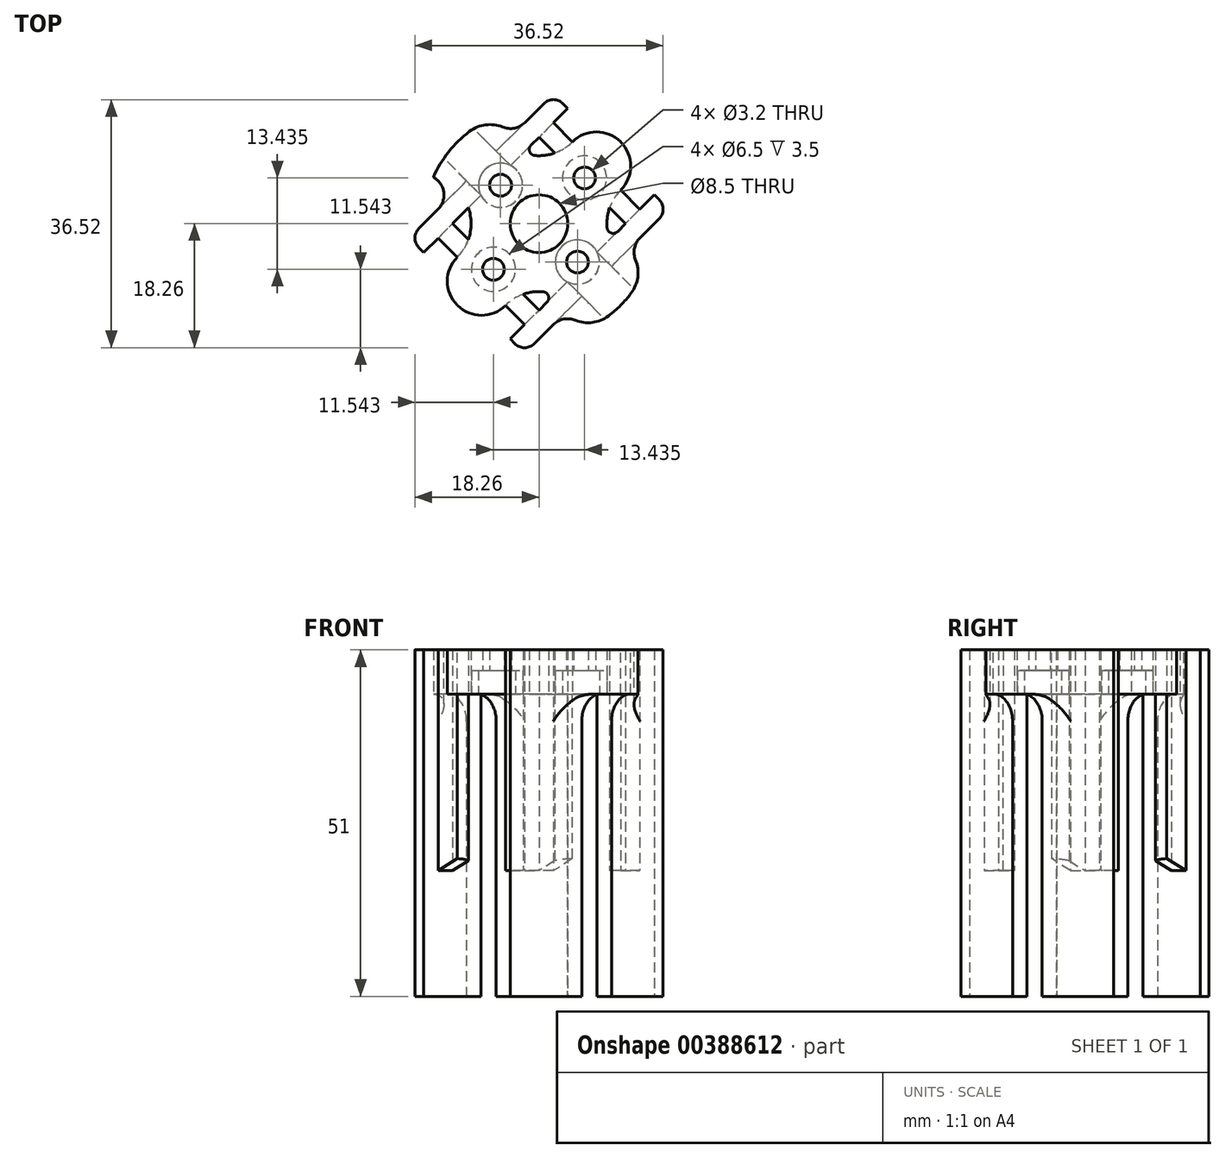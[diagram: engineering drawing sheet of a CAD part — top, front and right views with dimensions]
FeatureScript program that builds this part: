
annotation { "Feature Type Name" : "Feature", "Feature Type Description" : "" }
export const myFeature = defineFeature(function(context is Context, id is Id, definition is map)
    precondition{}
    {
        {
            assignVariable(context, id + "F0", {"name" : "wrapAroundLength", "anyValue" : 46});
        }
        {
            assignVariable(context, id + "F1", {"name" : "screwHeadDepth", "anyValue" : 3.5});
        }
        {
            var Q0;
            Q0=qCreatedBy(makeId("Top.planeOp"),FACE);
            var sketch = newSketch(context, id + "F2", { "sketchPlane" : qUnion([Q0])});
            skCircle(sketch, "E0", {"center": v(0, 0) * mm, "radius": 17 * mm});
            skLineSegment(sketch, "E1", {"start": v(0, 0) * mm, "end": v(-12.02, -12.02) * mm});
            skLineSegment(sketch, "E2", {"start": v(0, 0) * mm, "end": v(12.02, -12.02) * mm});
            skLineSegment(sketch, "E3", {"start": v(0, 0) * mm, "end": v(-12.02, 12.02) * mm});
            skLineSegment(sketch, "E4", {"start": v(0, 0) * mm, "end": v(12.02, 12.02) * mm});
            skCircle(sketch, "E5", {"center": v(-6.72, -6.72) * mm, "radius": 1.6 * mm});
            skCircle(sketch, "E6", {"center": v(6.72, 6.72) * mm, "radius": 1.6 * mm});
            skCircle(sketch, "E7", {"center": v(5.66, -5.66) * mm, "radius": 1.6 * mm});
            skCircle(sketch, "E8", {"center": v(-5.66, 5.66) * mm, "radius": 1.6 * mm});
            skCircle(sketch, "E9", {"center": v(0, 0) * mm, "radius": 4.25 * mm});
            skArc(sketch, "E10", {"start": v(-6.85, 15.56) * mm, "mid": v(0, 10) * mm, "end": v(6.85, 15.56) * mm});
            skArc(sketch, "E11", {"start": v(15.56, 6.85) * mm, "mid": v(10, 0) * mm, "end": v(15.56, -6.85) * mm});
            skArc(sketch, "E12", {"start": v(6.85, -15.56) * mm, "mid": v(0, -10) * mm, "end": v(-6.85, -15.56) * mm});
            skArc(sketch, "E13", {"start": v(-15.56, -6.85) * mm, "mid": v(-10, 0) * mm, "end": v(-15.56, 6.85) * mm});
            skSolve(sketch);
        }
        {
            var Q0;
            {var subQ10=sQuery(id+"F2.wireOp",EDGE,"E11");Q0=makeQuery(id+"F2.imprint","IMPRINT",FACE,{"disambiguationData":[TD([[makeQuery(id+"F2.imprint","IMPRINT",EDGE,{"derivedFrom":subQ10}),-1.0]])]});}
            var Q1;
            {var subQ7=sQuery(id+"F2.wireOp",EDGE,"E10");Q1=makeQuery(id+"F2.imprint","IMPRINT",FACE,{"disambiguationData":[TD([[makeQuery(id+"F2.imprint","IMPRINT",EDGE,{"derivedFrom":subQ7}),-1.0]])]});}
            var Q2;
            {var subQ7=sQuery(id+"F2.wireOp",EDGE,"pa5JDaWK-p0si-kU4j-njws-uxYAEp68zFFt");Q2=makeQuery(id+"F2.imprint","IMPRINT",FACE,{"disambiguationData":[TD([[makeQuery(id+"F2.imprint","IMPRINT",EDGE,{"derivedFrom":subQ7}),-1.0]])]});}
            var Q3;
            {var subQ10=sQuery(id+"F2.wireOp",EDGE,"E12");Q3=makeQuery(id+"F2.imprint","IMPRINT",FACE,{"disambiguationData":[TD([[makeQuery(id+"F2.imprint","IMPRINT",EDGE,{"derivedFrom":subQ10}),-1.0]])]});}
            var Q4;
            {var subQ7=sQuery(id+"F2.wireOp",EDGE,"E13");Q4=makeQuery(id+"F2.imprint","IMPRINT",FACE,{"disambiguationData":[TD([[makeQuery(id+"F2.imprint","IMPRINT",EDGE,{"derivedFrom":subQ7}),-1.0]])]});}
            extrude(context, id + "F3", {"entities" : qUnion([Q0, Q1, Q2, Q3, Q4]), "depth" : (getVariable(context, 'screwHeadDepth')) * mm + 3 * mm});
        }
        {
            var Q0;
            Q0=makeQuery(id+"F3.opExtrude","CAP_FACE",FACE,{"disambiguationData":[OSD([sQuery(id+"F2.wireOp",EDGE,"E0"),sQuery(id+"F2.wireOp",EDGE,"E5"),sQuery(id+"F2.wireOp",EDGE,"E6"),sQuery(id+"F2.wireOp",EDGE,"E7"),sQuery(id+"F2.wireOp",EDGE,"E8"),sQuery(id+"F2.wireOp",EDGE,"E9")])],"isStart":true});
            var sketch = newSketch(context, id + "F4", { "sketchPlane" : qUnion([Q0])});
            skCircle(sketch, "E14", {"center": v(-6.72, 6.72) * mm, "radius": 3.25 * mm});
            skCircle(sketch, "E15", {"center": v(-5.66, -5.66) * mm, "radius": 3.25 * mm});
            skCircle(sketch, "E16", {"center": v(5.66, 5.66) * mm, "radius": 3.25 * mm});
            skCircle(sketch, "E17", {"center": v(6.72, -6.72) * mm, "radius": 3.25 * mm});
            skSolve(sketch);
        }
        {
            var Q0;
            Q0=qSketchRegion(id+"F4",true);
            extrude(context, id + "F5", {"entities" : qUnion([Q0]), "operationType" : NewBodyOperationType.REMOVE, "oppositeDirection" : true, "depth" : (getVariable(context, 'screwHeadDepth')) * mm});
        }
        {
            var Q0;
            Q0=qCreatedBy(makeId("Top.planeOp"),FACE);
            var sketch = newSketch(context, id + "F6", { "sketchPlane" : qUnion([Q0])});
            skLineSegment(sketch, "E18", {"start": v(-5.97, 5.97) * mm, "end": v(-5.97, 5.97) * mm});
            skLineSegment(sketch, "E19", {"start": v(0, 0) * mm, "end": v(-34.06, 34.06) * mm, "construction": true});
            skLineSegment(sketch, "E20", {"start": v(0, 0) * mm, "end": v(34.06, -34.06) * mm, "construction": true});
            skLineSegment(sketch, "E21", {"start": v(0, 0) * mm, "end": v(25.74, 25.74) * mm, "construction": true});
            skLineSegment(sketch, "E22", {"start": v(0, 0) * mm, "end": v(-25.74, -25.74) * mm, "construction": true});
            skLineSegment(sketch, "E23", {"start": v(-8.55, 4.18) * mm, "end": v(-16.97, -4.24) * mm});
            skLineSegment(sketch, "E24", {"start": v(-16.97, -4.24) * mm, "end": v(-19.1, -2.12) * mm});
            skLineSegment(sketch, "E25", {"start": v(-19.1, -2.12) * mm, "end": v(-10.67, 6.3) * mm});
            skCircle(sketch, "E26.0", {"center": v(-5.66, 5.66) * mm, "radius": 3.25 * mm});
            skLineSegment(sketch, "E27.MirrorCS", {"start": v(2.12, 19.1) * mm, "end": v(-6.3, 10.67) * mm});
            skLineSegment(sketch, "E28.MirrorCS", {"start": v(-4.18, 8.55) * mm, "end": v(4.24, 16.97) * mm});
            skLineSegment(sketch, "E29.MirrorCS", {"start": v(4.24, 16.97) * mm, "end": v(2.12, 19.1) * mm});
            skLineSegment(sketch, "E30.MirrorCS", {"start": v(4.18, -8.55) * mm, "end": v(-4.24, -16.97) * mm});
            skLineSegment(sketch, "E31.MirrorCS", {"start": v(-4.24, -16.97) * mm, "end": v(-2.12, -19.1) * mm});
            skLineSegment(sketch, "E32.MirrorCS", {"start": v(-2.12, -19.1) * mm, "end": v(6.3, -10.67) * mm});
            skLineSegment(sketch, "E33.MirrorCS", {"start": v(19.1, 2.12) * mm, "end": v(10.67, -6.3) * mm});
            skLineSegment(sketch, "E34.MirrorCS", {"start": v(8.55, -4.18) * mm, "end": v(16.97, 4.24) * mm});
            skLineSegment(sketch, "E35.MirrorCS", {"start": v(16.97, 4.24) * mm, "end": v(19.1, 2.12) * mm});
            skCircle(sketch, "E36.0", {"center": v(5.66, -5.66) * mm, "radius": 3.25 * mm});
            skLineSegment(sketch, "E37", {"start": v(10.67, -6.3) * mm, "end": v(6.3, -10.67) * mm});
            skLineSegment(sketch, "E38", {"start": v(-10.67, 6.3) * mm, "end": v(-6.3, 10.67) * mm});
            skLineSegment(sketch, "E39", {"start": v(-8.55, 4.18) * mm, "end": v(-10.67, 6.3) * mm});
            skLineSegment(sketch, "E40", {"start": v(-6.3, 10.67) * mm, "end": v(-4.18, 8.55) * mm});
            skLineSegment(sketch, "E41", {"start": v(8.55, -4.18) * mm, "end": v(10.67, -6.3) * mm});
            skLineSegment(sketch, "E42", {"start": v(6.3, -10.67) * mm, "end": v(4.18, -8.55) * mm});
            skSolve(sketch);
        }
        {
            var Q0;
            {var subQ0=sQuery(id+"F6.wireOp",EDGE,"E23");Q0=makeQuery(id+"F6.imprint","IMPRINT",FACE,{"disambiguationData":[TD([[makeQuery(id+"F6.imprint","IMPRINT",EDGE,{"derivedFrom":subQ0}),-1.0]])]});}
            var Q1;
            {var subQ0=sQuery(id+"F6.wireOp",EDGE,"E27.MirrorCS");Q1=makeQuery(id+"F6.imprint","IMPRINT",FACE,{"disambiguationData":[TD([[makeQuery(id+"F6.imprint","IMPRINT",EDGE,{"derivedFrom":subQ0}),1.0]])]});}
            var Q2;
            {var subQ0=sQuery(id+"F6.wireOp",EDGE,"E33.MirrorCS");Q2=makeQuery(id+"F6.imprint","IMPRINT",FACE,{"disambiguationData":[TD([[makeQuery(id+"F6.imprint","IMPRINT",EDGE,{"derivedFrom":subQ0}),-1.0]])]});}
            var Q3;
            {var subQ0=sQuery(id+"F6.wireOp",EDGE,"E30.MirrorCS");Q3=makeQuery(id+"F6.imprint","IMPRINT",FACE,{"disambiguationData":[TD([[makeQuery(id+"F6.imprint","IMPRINT",EDGE,{"derivedFrom":subQ0}),1.0]])]});}
            extrude(context, id + "F7", {"entities" : qUnion([Q0, Q1, Q2, Q3]), "operationType" : NewBodyOperationType.ADD, "depth" : (getVariable(context, 'screwHeadDepth')) * mm + 3 * mm, "hasSecondDirection" : true, "secondDirectionOppositeDirection" : true, "secondDirectionDepth" : (getVariable(context, 'wrapAroundLength')) * mm - (getVariable(context, 'screwHeadDepth')) * mm + 2 * mm});
        }
        {
            var Q0;
            Q0=makeQuery(id+"F7.boolean.opBoolean","INTERSECT",EDGE,{"derivedFrom":[makeQuery(id+"F3.opExtrude","SWEPT_FACE",FACE,{"disambiguationData":[OSD([sQuery(id+"F2.wireOp",EDGE,"E11")])]}),makeQuery(id+"F7.opExtrude","SWEPT_FACE",FACE,{"disambiguationData":[OSD([sQuery(id+"F6.wireOp",EDGE,"E33.MirrorCS")])]})]});
            var Q1;
            Q1=makeQuery(id+"F7.boolean.opBoolean","INTERSECT",EDGE,{"derivedFrom":[makeQuery(id+"F3.opExtrude","SWEPT_FACE",FACE,{"disambiguationData":[OSD([sQuery(id+"F2.wireOp",EDGE,"E12")])]}),makeQuery(id+"F7.opExtrude","SWEPT_FACE",FACE,{"disambiguationData":[OSD([sQuery(id+"F6.wireOp",EDGE,"E32.MirrorCS")])]})]});
            var Q2;
            Q2=makeQuery(id+"F7.boolean.opBoolean","INTERSECT",EDGE,{"derivedFrom":[makeQuery(id+"F3.opExtrude","SWEPT_FACE",FACE,{"disambiguationData":[OSD([sQuery(id+"F2.wireOp",EDGE,"E13")])]}),makeQuery(id+"F7.opExtrude","SWEPT_FACE",FACE,{"disambiguationData":[OSD([sQuery(id+"F6.wireOp",EDGE,"E25"),sQuery(id+"F6.wireOp",EDGE,"E27.MirrorCS"),sQuery(id+"F6.wireOp",EDGE,"E38")])]})]});
            var Q3;
            Q3=makeQuery(id+"F7.boolean.opBoolean","INTERSECT",EDGE,{"derivedFrom":[makeQuery(id+"F3.opExtrude","SWEPT_FACE",FACE,{"disambiguationData":[OSD([sQuery(id+"F2.wireOp",EDGE,"E10")])]}),makeQuery(id+"F7.opExtrude","SWEPT_FACE",FACE,{"disambiguationData":[OSD([sQuery(id+"F6.wireOp",EDGE,"E25"),sQuery(id+"F6.wireOp",EDGE,"E27.MirrorCS"),sQuery(id+"F6.wireOp",EDGE,"E38")])]})]});
            fillet(context, id + "F8", {"entities" : qUnion([Q0, Q1, Q2, Q3]), "radius" : 3 * mm, "tangentPropagation" : true, "allowEdgeOverflow" : false});
        }
        {
            var Q0;
            Q0=makeQuery(id+"F7.boolean.opBoolean","INTERSECT",EDGE,{"derivedFrom":[makeQuery(id+"F3.opExtrude","SWEPT_FACE",FACE,{"disambiguationData":[OSD([sQuery(id+"F2.wireOp",EDGE,"E11")])]}),makeQuery(id+"F7.opExtrude","SWEPT_FACE",FACE,{"disambiguationData":[OSD([sQuery(id+"F6.wireOp",EDGE,"E34.MirrorCS")])]})]});
            var Q1;
            Q1=makeQuery(id+"F7.boolean.opBoolean","INTERSECT",EDGE,{"derivedFrom":[makeQuery(id+"F3.opExtrude","SWEPT_FACE",FACE,{"disambiguationData":[OSD([sQuery(id+"F2.wireOp",EDGE,"E12")])]}),makeQuery(id+"F7.opExtrude","SWEPT_FACE",FACE,{"disambiguationData":[OSD([sQuery(id+"F6.wireOp",EDGE,"E30.MirrorCS")])]})]});
            var Q2;
            Q2=makeQuery(id+"F7.boolean.opBoolean","INTERSECT",EDGE,{"derivedFrom":[makeQuery(id+"F3.opExtrude","SWEPT_FACE",FACE,{"disambiguationData":[OSD([sQuery(id+"F2.wireOp",EDGE,"E10")])]}),makeQuery(id+"F7.opExtrude","SWEPT_FACE",FACE,{"disambiguationData":[OSD([sQuery(id+"F6.wireOp",EDGE,"E28.MirrorCS")])]})]});
            var Q3;
            Q3=makeQuery(id+"F7.boolean.opBoolean","INTERSECT",EDGE,{"derivedFrom":[makeQuery(id+"F3.opExtrude","SWEPT_FACE",FACE,{"disambiguationData":[OSD([sQuery(id+"F2.wireOp",EDGE,"pa5JDaWK-p0si-kU4j-njws-uxYAEp68zFFt")])]}),makeQuery(id+"F7.opExtrude","SWEPT_FACE",FACE,{"disambiguationData":[OSD([sQuery(id+"F6.wireOp",EDGE,"E23")])]})]});
            fillet(context, id + "F9", {"entities" : qUnion([Q0, Q1, Q2, Q3]), "radius" : 0.9 * mm, "tangentPropagation" : true, "allowEdgeOverflow" : false});
        }
        {
            var Q0;
            {var subQ0=sQuery(id+"F2.wireOp",EDGE,"E11");var subQ1=sQuery(id+"F2.wireOp",EDGE,"E0");Q0=makeQuery(id+"F3.opExtrude","SWEPT_EDGE",EDGE,{"disambiguationData":[OSD([subQ1,subQ0]),TDD([makeQuery(id+"F2.imprint","INTERSECT",VERTEX,{"disambiguationData":[OD(0.0)],"derivedFrom":[subQ1,subQ0]})])]});}
            var Q1;
            {var subQ0=sQuery(id+"F2.wireOp",EDGE,"E10");var subQ1=sQuery(id+"F2.wireOp",EDGE,"E0");Q1=makeQuery(id+"F3.opExtrude","SWEPT_EDGE",EDGE,{"disambiguationData":[OSD([subQ1,subQ0]),TDD([makeQuery(id+"F2.imprint","INTERSECT",VERTEX,{"disambiguationData":[OD(1.0)],"derivedFrom":[subQ1,subQ0]})])]});}
            var Q2;
            {var subQ0=sQuery(id+"F2.wireOp",EDGE,"E12");var subQ1=sQuery(id+"F2.wireOp",EDGE,"E0");Q2=makeQuery(id+"F3.opExtrude","SWEPT_EDGE",EDGE,{"disambiguationData":[OSD([subQ1,subQ0]),TDD([makeQuery(id+"F2.imprint","INTERSECT",VERTEX,{"disambiguationData":[OD(1.0)],"derivedFrom":[subQ1,subQ0]})])]});}
            var Q3;
            {var subQ0=sQuery(id+"F2.wireOp",EDGE,"pa5JDaWK-p0si-kU4j-njws-uxYAEp68zFFt");var subQ1=sQuery(id+"F2.wireOp",EDGE,"E0");Q3=makeQuery(id+"F3.opExtrude","SWEPT_EDGE",EDGE,{"disambiguationData":[OSD([subQ1,subQ0]),TDD([makeQuery(id+"F2.imprint","INTERSECT",VERTEX,{"disambiguationData":[OD(0.0)],"derivedFrom":[subQ1,subQ0]})])]});}
            var Q4;
            {var subQ0=sQuery(id+"F2.wireOp",EDGE,"E0");var subQ1=makeQuery(id+"F2.imprint","INTERSECT",VERTEX,{"derivedFrom":[subQ0,sQuery(id+"F2.wireOp",EDGE,"E2")]});var subQ2=sQuery(id+"F2.wireOp",EDGE,"E11");Q4=makeQuery(id+"F8.opFillet","BLEND_EDGE",EDGE,{"blendedFrom":[makeQuery(id+"F7.boolean.opBoolean","INTERSECT",EDGE,{"derivedFrom":[makeQuery(id+"F3.opExtrude","SWEPT_FACE",FACE,{"disambiguationData":[OSD([subQ2])]}),makeQuery(id+"F7.opExtrude","SWEPT_FACE",FACE,{"disambiguationData":[OSD([sQuery(id+"F6.wireOp",EDGE,"E33.MirrorCS")])]})]}),makeQuery(id+"F3.opExtrude","SWEPT_FACE",FACE,{"disambiguationData":[OSD([subQ0]),TDD([makeQuery(id+"F2.imprint","IMPRINT",EDGE,{"disambiguationData":[TD([[subQ1,1.0]])],"derivedFrom":subQ0}),makeQuery(id+"F2.imprint","IMPRINT",EDGE,{"disambiguationData":[TD([[subQ1,-1.0]])],"derivedFrom":subQ0})])]})],"blendedInto":[makeQuery(id+"F3.opExtrude","SWEPT_FACE",FACE,{"disambiguationData":[OSD([subQ0]),TDD([makeQuery(id+"F2.imprint","IMPRINT",EDGE,{"disambiguationData":[TD([[subQ1,1.0]])],"derivedFrom":subQ0}),makeQuery(id+"F2.imprint","IMPRINT",EDGE,{"disambiguationData":[TD([[subQ1,-1.0]])],"derivedFrom":subQ0})])]})]});}
            var Q5;
            {var subQ0=sQuery(id+"F2.wireOp",EDGE,"E0");var subQ1=makeQuery(id+"F2.imprint","INTERSECT",VERTEX,{"derivedFrom":[subQ0,sQuery(id+"F2.wireOp",EDGE,"E2")]});var subQ2=sQuery(id+"F2.wireOp",EDGE,"E12");Q5=makeQuery(id+"F8.opFillet","BLEND_EDGE",EDGE,{"blendedFrom":[makeQuery(id+"F7.boolean.opBoolean","INTERSECT",EDGE,{"derivedFrom":[makeQuery(id+"F3.opExtrude","SWEPT_FACE",FACE,{"disambiguationData":[OSD([subQ2])]}),makeQuery(id+"F7.opExtrude","SWEPT_FACE",FACE,{"disambiguationData":[OSD([sQuery(id+"F6.wireOp",EDGE,"E32.MirrorCS")])]})]}),makeQuery(id+"F3.opExtrude","SWEPT_FACE",FACE,{"disambiguationData":[OSD([subQ0]),TDD([makeQuery(id+"F2.imprint","IMPRINT",EDGE,{"disambiguationData":[TD([[subQ1,1.0]])],"derivedFrom":subQ0}),makeQuery(id+"F2.imprint","IMPRINT",EDGE,{"disambiguationData":[TD([[subQ1,-1.0]])],"derivedFrom":subQ0})])]})],"blendedInto":[makeQuery(id+"F3.opExtrude","SWEPT_FACE",FACE,{"disambiguationData":[OSD([subQ0]),TDD([makeQuery(id+"F2.imprint","IMPRINT",EDGE,{"disambiguationData":[TD([[subQ1,1.0]])],"derivedFrom":subQ0}),makeQuery(id+"F2.imprint","IMPRINT",EDGE,{"disambiguationData":[TD([[subQ1,-1.0]])],"derivedFrom":subQ0})])]})]});}
            var Q6;
            {var subQ0=sQuery(id+"F2.wireOp",EDGE,"E0");var subQ1=makeQuery(id+"F2.imprint","INTERSECT",VERTEX,{"derivedFrom":[subQ0,sQuery(id+"F2.wireOp",EDGE,"E3")]});var subQ2=sQuery(id+"F2.wireOp",EDGE,"pa5JDaWK-p0si-kU4j-njws-uxYAEp68zFFt");Q6=makeQuery(id+"F8.opFillet","BLEND_EDGE",EDGE,{"blendedFrom":[makeQuery(id+"F7.boolean.opBoolean","INTERSECT",EDGE,{"derivedFrom":[makeQuery(id+"F3.opExtrude","SWEPT_FACE",FACE,{"disambiguationData":[OSD([subQ2])]}),makeQuery(id+"F7.opExtrude","SWEPT_FACE",FACE,{"disambiguationData":[OSD([sQuery(id+"F6.wireOp",EDGE,"E25")])]})]}),makeQuery(id+"F3.opExtrude","SWEPT_FACE",FACE,{"disambiguationData":[OSD([subQ0]),TDD([makeQuery(id+"F2.imprint","IMPRINT",EDGE,{"disambiguationData":[TD([[subQ1,1.0]])],"derivedFrom":subQ0}),makeQuery(id+"F2.imprint","IMPRINT",EDGE,{"disambiguationData":[TD([[subQ1,-1.0]])],"derivedFrom":subQ0})])]})],"blendedInto":[makeQuery(id+"F3.opExtrude","SWEPT_FACE",FACE,{"disambiguationData":[OSD([subQ0]),TDD([makeQuery(id+"F2.imprint","IMPRINT",EDGE,{"disambiguationData":[TD([[subQ1,1.0]])],"derivedFrom":subQ0}),makeQuery(id+"F2.imprint","IMPRINT",EDGE,{"disambiguationData":[TD([[subQ1,-1.0]])],"derivedFrom":subQ0})])]})]});}
            var Q7;
            {var subQ0=sQuery(id+"F2.wireOp",EDGE,"E0");var subQ1=makeQuery(id+"F2.imprint","INTERSECT",VERTEX,{"derivedFrom":[subQ0,sQuery(id+"F2.wireOp",EDGE,"E3")]});var subQ2=sQuery(id+"F2.wireOp",EDGE,"E10");Q7=makeQuery(id+"F8.opFillet","BLEND_EDGE",EDGE,{"blendedFrom":[makeQuery(id+"F7.boolean.opBoolean","INTERSECT",EDGE,{"derivedFrom":[makeQuery(id+"F3.opExtrude","SWEPT_FACE",FACE,{"disambiguationData":[OSD([subQ2])]}),makeQuery(id+"F7.opExtrude","SWEPT_FACE",FACE,{"disambiguationData":[OSD([sQuery(id+"F6.wireOp",EDGE,"E27.MirrorCS")])]})]}),makeQuery(id+"F3.opExtrude","SWEPT_FACE",FACE,{"disambiguationData":[OSD([subQ0]),TDD([makeQuery(id+"F2.imprint","IMPRINT",EDGE,{"disambiguationData":[TD([[subQ1,1.0]])],"derivedFrom":subQ0}),makeQuery(id+"F2.imprint","IMPRINT",EDGE,{"disambiguationData":[TD([[subQ1,-1.0]])],"derivedFrom":subQ0})])]})],"blendedInto":[makeQuery(id+"F3.opExtrude","SWEPT_FACE",FACE,{"disambiguationData":[OSD([subQ0]),TDD([makeQuery(id+"F2.imprint","IMPRINT",EDGE,{"disambiguationData":[TD([[subQ1,1.0]])],"derivedFrom":subQ0}),makeQuery(id+"F2.imprint","IMPRINT",EDGE,{"disambiguationData":[TD([[subQ1,-1.0]])],"derivedFrom":subQ0})])]})]});}
            var Q8;
            {var subQ0=sQuery(id+"F2.wireOp",EDGE,"E13");var subQ1=sQuery(id+"F2.wireOp",EDGE,"E0");Q8=makeQuery(id+"F3.opExtrude","SWEPT_EDGE",EDGE,{"disambiguationData":[OSD([subQ1,subQ0]),TDD([makeQuery(id+"F2.imprint","INTERSECT",VERTEX,{"disambiguationData":[OD(0.0)],"derivedFrom":[subQ1,subQ0]})])]});}
            fillet(context, id + "F10", {"entities" : qUnion([Q0, Q1, Q2, Q3, Q4, Q5, Q6, Q7, Q8]), "radius" : 5 * mm, "tangentPropagation" : true, "allowEdgeOverflow" : false});
        }
        {
            var Q0;
            Q0=makeQuery(id+"F7.boolean.opBoolean","INTERSECT",EDGE,{"derivedFrom":[makeQuery(id+"F3.opExtrude","CAP_FACE",FACE,{"disambiguationData":[OSD([sQuery(id+"F2.wireOp",EDGE,"E0"),sQuery(id+"F2.wireOp",EDGE,"E5"),sQuery(id+"F2.wireOp",EDGE,"E6"),sQuery(id+"F2.wireOp",EDGE,"E7"),sQuery(id+"F2.wireOp",EDGE,"E8"),sQuery(id+"F2.wireOp",EDGE,"E9"),sQuery(id+"F2.wireOp",EDGE,"E10"),sQuery(id+"F2.wireOp",EDGE,"E11"),sQuery(id+"F2.wireOp",EDGE,"E12"),sQuery(id+"F2.wireOp",EDGE,"E13")])],"isStart":true}),makeQuery(id+"F7.opExtrude","SWEPT_FACE",FACE,{"disambiguationData":[OSD([sQuery(id+"F6.wireOp",EDGE,"E25")])]})]});
            var Q1;
            Q1=makeQuery(id+"F7.boolean.opBoolean","INTERSECT",EDGE,{"derivedFrom":[makeQuery(id+"F3.opExtrude","CAP_FACE",FACE,{"disambiguationData":[OSD([sQuery(id+"F2.wireOp",EDGE,"E0"),sQuery(id+"F2.wireOp",EDGE,"E5"),sQuery(id+"F2.wireOp",EDGE,"E6"),sQuery(id+"F2.wireOp",EDGE,"E7"),sQuery(id+"F2.wireOp",EDGE,"E8"),sQuery(id+"F2.wireOp",EDGE,"E9"),sQuery(id+"F2.wireOp",EDGE,"E10"),sQuery(id+"F2.wireOp",EDGE,"E11"),sQuery(id+"F2.wireOp",EDGE,"E12"),sQuery(id+"F2.wireOp",EDGE,"E13")])],"isStart":true}),makeQuery(id+"F7.opExtrude","SWEPT_FACE",FACE,{"disambiguationData":[OSD([sQuery(id+"F6.wireOp",EDGE,"E27.MirrorCS")])]})]});
            var Q2;
            Q2=makeQuery(id+"F7.boolean.opBoolean","INTERSECT",EDGE,{"derivedFrom":[makeQuery(id+"F3.opExtrude","CAP_FACE",FACE,{"disambiguationData":[OSD([sQuery(id+"F2.wireOp",EDGE,"E0"),sQuery(id+"F2.wireOp",EDGE,"E5"),sQuery(id+"F2.wireOp",EDGE,"E6"),sQuery(id+"F2.wireOp",EDGE,"E7"),sQuery(id+"F2.wireOp",EDGE,"E8"),sQuery(id+"F2.wireOp",EDGE,"E9"),sQuery(id+"F2.wireOp",EDGE,"E10"),sQuery(id+"F2.wireOp",EDGE,"E11"),sQuery(id+"F2.wireOp",EDGE,"E12"),sQuery(id+"F2.wireOp",EDGE,"E13")])],"isStart":true}),makeQuery(id+"F7.opExtrude","SWEPT_FACE",FACE,{"disambiguationData":[OSD([sQuery(id+"F6.wireOp",EDGE,"E32.MirrorCS")])]})]});
            var Q3;
            Q3=makeQuery(id+"F7.boolean.opBoolean","INTERSECT",EDGE,{"derivedFrom":[makeQuery(id+"F3.opExtrude","CAP_FACE",FACE,{"disambiguationData":[OSD([sQuery(id+"F2.wireOp",EDGE,"E0"),sQuery(id+"F2.wireOp",EDGE,"E5"),sQuery(id+"F2.wireOp",EDGE,"E6"),sQuery(id+"F2.wireOp",EDGE,"E7"),sQuery(id+"F2.wireOp",EDGE,"E8"),sQuery(id+"F2.wireOp",EDGE,"E9"),sQuery(id+"F2.wireOp",EDGE,"E10"),sQuery(id+"F2.wireOp",EDGE,"E11"),sQuery(id+"F2.wireOp",EDGE,"E12"),sQuery(id+"F2.wireOp",EDGE,"E13")])],"isStart":true}),makeQuery(id+"F7.opExtrude","SWEPT_FACE",FACE,{"disambiguationData":[OSD([sQuery(id+"F6.wireOp",EDGE,"E33.MirrorCS")])]})]});
            fillet(context, id + "F11", {"entities" : qUnion([Q0, Q1, Q2, Q3]), "radius" : 4 * mm, "tangentPropagation" : true, "allowEdgeOverflow" : false});
        }
        {
            var Q0;
            Q0=makeQuery(id+"F7.opExtrude","SWEPT_EDGE",EDGE,{"disambiguationData":[OSD([sQuery(id+"F6.wireOp",EDGE,"E31.MirrorCS"),sQuery(id+"F6.wireOp",EDGE,"E32.MirrorCS")])]});
            var Q1;
            Q1=makeQuery(id+"F7.opExtrude","SWEPT_EDGE",EDGE,{"disambiguationData":[OSD([sQuery(id+"F6.wireOp",EDGE,"E33.MirrorCS"),sQuery(id+"F6.wireOp",EDGE,"E35.MirrorCS")])]});
            var Q2;
            Q2=makeQuery(id+"F7.opExtrude","SWEPT_EDGE",EDGE,{"disambiguationData":[OSD([sQuery(id+"F6.wireOp",EDGE,"E27.MirrorCS"),sQuery(id+"F6.wireOp",EDGE,"E29.MirrorCS")])]});
            var Q3;
            Q3=makeQuery(id+"F7.opExtrude","SWEPT_EDGE",EDGE,{"disambiguationData":[OSD([sQuery(id+"F6.wireOp",EDGE,"E24"),sQuery(id+"F6.wireOp",EDGE,"E25")])]});
            fillet(context, id + "F12", {"entities" : qUnion([Q0, Q1, Q2, Q3]), "radius" : 2 * mm, "tangentPropagation" : true, "allowEdgeOverflow" : false});
        }
        {
            var Q0;
            Q0=qCreatedBy(makeId("Top.planeOp"),FACE);
            var sketch = newSketch(context, id + "F13", { "sketchPlane" : qUnion([Q0])});
            skLineSegment(sketch, "E43", {"start": v(-4.94, -12.04) * mm, "end": v(-2.12, -14.85) * mm});
            skLineSegment(sketch, "E44", {"start": v(0, -12.73) * mm, "end": v(-2.33, -10.4) * mm});
            skLineSegment(sketch, "E45", {"start": v(-2.12, -14.85) * mm, "end": v(0, -12.73) * mm});
            skArc(sketch, "E46.0", {"start": v(0.61, -10.03) * mm, "mid": v(-2.39, -10.42) * mm, "end": v(-4.94, -12.04) * mm});
            skArc(sketch, "E46.1", {"start": v(-4.94, -12.04) * mm, "mid": v(-8.47, -13.5) * mm, "end": v(-12, -12.04) * mm});
            skLineSegment(sketch, "E47", {"start": v(0, 0) * mm, "end": v(-11.26, -11.26) * mm, "construction": true});
            skLineSegment(sketch, "E48", {"start": v(0, 0) * mm, "end": v(14.48, 14.48) * mm, "construction": true});
            skLineSegment(sketch, "E49", {"start": v(0, 0) * mm, "end": v(-10.6, 10.6) * mm, "construction": true});
            skLineSegment(sketch, "E50", {"start": v(0, 0) * mm, "end": v(8.15, -8.15) * mm, "construction": true});
            skLineSegment(sketch, "E51.MirrorCS", {"start": v(12.73, 0) * mm, "end": v(10.4, 2.33) * mm});
            skLineSegment(sketch, "E52.MirrorCS", {"start": v(12.04, 4.94) * mm, "end": v(14.85, 2.12) * mm});
            skLineSegment(sketch, "E53.MirrorCS", {"start": v(14.85, 2.12) * mm, "end": v(12.73, 0) * mm});
            skArc(sketch, "E54.MirrorCS", {"start": v(12.04, 4.94) * mm, "mid": v(13.5, 8.47) * mm, "end": v(12.04, 12) * mm});
            skArc(sketch, "E55.MirrorCS", {"start": v(10.03, -0.61) * mm, "mid": v(10.42, 2.39) * mm, "end": v(12.04, 4.94) * mm});
            skLineSegment(sketch, "E56.MirrorCS", {"start": v(-12.04, -4.94) * mm, "end": v(-14.85, -2.12) * mm});
            skLineSegment(sketch, "E57.MirrorCS", {"start": v(-12.73, 0) * mm, "end": v(-10.4, -2.33) * mm});
            skArc(sketch, "E58.MirrorCS", {"start": v(-10.03, 0.61) * mm, "mid": v(-10.42, -2.39) * mm, "end": v(-12.04, -4.94) * mm});
            skArc(sketch, "E59.MirrorCS", {"start": v(-12.04, -4.94) * mm, "mid": v(-13.5, -8.47) * mm, "end": v(-12.04, -12) * mm});
            skLineSegment(sketch, "E60.MirrorCS", {"start": v(-14.85, -2.12) * mm, "end": v(-12.73, 0) * mm});
            skLineSegment(sketch, "E61.MirrorCS", {"start": v(0, 12.73) * mm, "end": v(2.33, 10.4) * mm});
            skLineSegment(sketch, "E62.MirrorCS", {"start": v(4.94, 12.04) * mm, "end": v(2.12, 14.85) * mm});
            skArc(sketch, "E63.MirrorCS", {"start": v(4.94, 12.04) * mm, "mid": v(8.47, 13.5) * mm, "end": v(12, 12.04) * mm});
            skArc(sketch, "E64.MirrorCS", {"start": v(-0.61, 10.03) * mm, "mid": v(2.39, 10.42) * mm, "end": v(4.94, 12.04) * mm});
            skLineSegment(sketch, "E65.MirrorCS", {"start": v(2.12, 14.85) * mm, "end": v(0, 12.73) * mm});
            skSolve(sketch);
        }
        {
            var Q0;
            Q0 = qSketchRegion(id + "F13", true);
            var Q1;
            Q1=makeQuery(id+"F3.opExtrude","CAP_FACE",FACE,{"disambiguationData":[OSD([sQuery(id+"F2.wireOp",EDGE,"E0"),sQuery(id+"F2.wireOp",EDGE,"E5"),sQuery(id+"F2.wireOp",EDGE,"E6"),sQuery(id+"F2.wireOp",EDGE,"E7"),sQuery(id+"F2.wireOp",EDGE,"E8"),sQuery(id+"F2.wireOp",EDGE,"E9"),sQuery(id+"F2.wireOp",EDGE,"E10"),sQuery(id+"F2.wireOp",EDGE,"E11"),sQuery(id+"F2.wireOp",EDGE,"E12"),sQuery(id+"F2.wireOp",EDGE,"E13")])],"isStart":false});
            extrude(context, id + "F14", {"entities" : qUnion([Q0]), "operationType" : NewBodyOperationType.ADD, "endBound" : BoundingType.UP_TO_SURFACE, "endBoundEntityFace" : qUnion([Q1]), "depth" : 25 * mm, "hasSecondDirection" : true, "secondDirectionOppositeDirection" : true, "secondDirectionDepth" : 26 * mm});
        }
        {
            var Q0;
            Q0=makeQuery(id+"F14.opExtrude","SWEPT_FACE",FACE,{"disambiguationData":[OSD([sQuery(id+"F13.wireOp",EDGE,"E62.MirrorCS")])]});
            var sketch = newSketch(context, id + "F15", { "sketchPlane" : qUnion([Q0])});
            skLineSegment(sketch, "E66", {"start": v(-9, 0) * mm, "end": v(-9, -26) * mm});
            skLineSegment(sketch, "E67", {"start": v(-9, -26) * mm, "end": v(-9, -18) * mm});
            skLineSegment(sketch, "E68", {"start": v(-9, -18) * mm, "end": v(9, -26) * mm});
            skLineSegment(sketch, "E69", {"start": v(9, -26) * mm, "end": v(-9, -26) * mm});
            skSolve(sketch);
        }
        {
            var Q0;
            {var subQ0=sQuery(id+"F15.wireOp",EDGE,"E67");Q0=makeQuery(id+"F15.imprint","IMPRINT",FACE,{"disambiguationData":[TD([[makeQuery(id+"F15.imprint","IMPRINT",EDGE,{"derivedFrom":subQ0}),-1.0]])]});}
            var Q1;
            {var subQ0=sQuery(id+"F15.wireOp",EDGE,"E69");var subQ1=sQuery(id+"F15.wireOp",EDGE,"E68");var subQ2=sQuery(id+"F13.wireOp",EDGE,"E62.MirrorCS");var subQ3=makeQuery(id+"F15.imprint","INTERSECT",VERTEX,{"derivedFrom":[makeQuery(id+"F14.opExtrude","SWEPT_EDGE",EDGE,{"disambiguationData":[OSD([subQ2,sQuery(id+"F13.wireOp",EDGE,"E65.MirrorCS")])]}),subQ1,subQ0]});Q1=makeQuery(id+"F15.imprint","IMPRINT",FACE,{"disambiguationData":[TD([[makeQuery(id+"F15.imprint","IMPRINT",EDGE,{"disambiguationData":[TD([[subQ3,1.0]])],"derivedFrom":subQ1}),-1.0]])]});}
            extrude(context, id + "F16", {"entities" : qUnion([Q0, Q1]), "operationType" : NewBodyOperationType.REMOVE, "endBound" : BoundingType.THROUGH_ALL, "oppositeDirection" : true, "depth" : 25 * mm});
        }
    });
